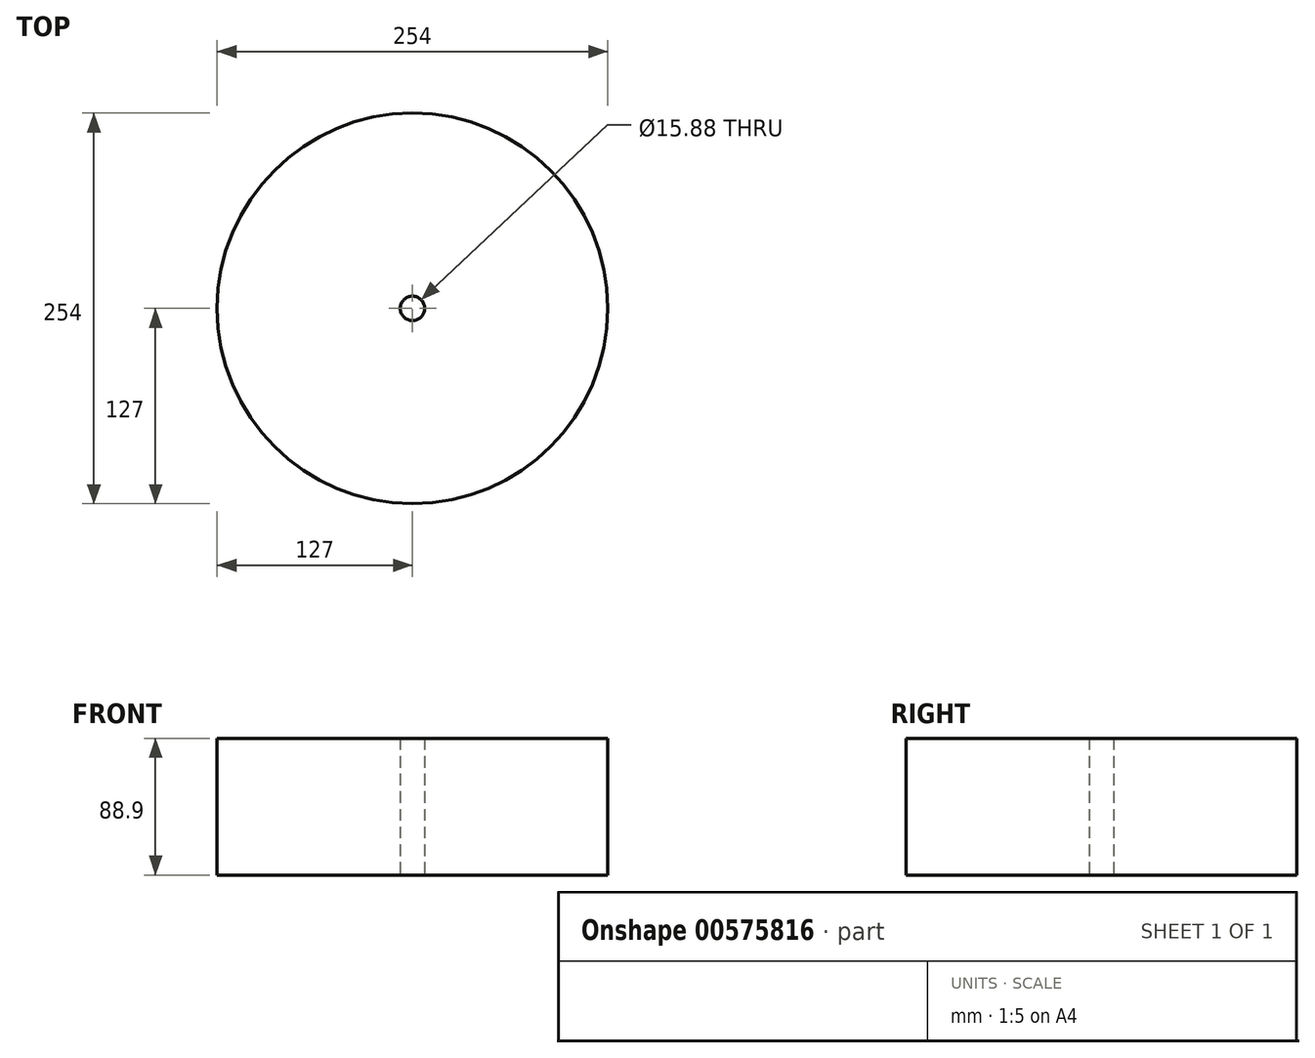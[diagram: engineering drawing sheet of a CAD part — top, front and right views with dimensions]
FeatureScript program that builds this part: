
annotation { "Feature Type Name" : "Feature", "Feature Type Description" : "" }
export const myFeature = defineFeature(function(context is Context, id is Id, definition is map)
    precondition{}
    {
        {
            var Q0;
            Q0=qCreatedBy(makeId("Top.planeOp"),FACE);
            var sketch = newSketch(context, id + "F0", { "sketchPlane" : qUnion([Q0])});
            skCircle(sketch, "E0", {"center": v(0, 0) * mm, "radius": 127 * mm});
            skCircle(sketch, "E1", {"center": v(0, 0) * mm, "radius": 7.94 * mm});
            skSolve(sketch);
        }
        {
            var Q0;
            Q0=makeQuery(id+"F0.imprint","IMPRINT",FACE,{"disambiguationData":[TD([[makeQuery(id+"F0.imprint","IMPRINT",EDGE,{"derivedFrom":sQuery(id+"F0.wireOp",EDGE,"E0")}),1.0]])]});
            extrude(context, id + "F1", {"entities" : qUnion([Q0]), "depth" : 88.9 * mm, "offsetDistance" : 25.4 * mm});
        }
    });
